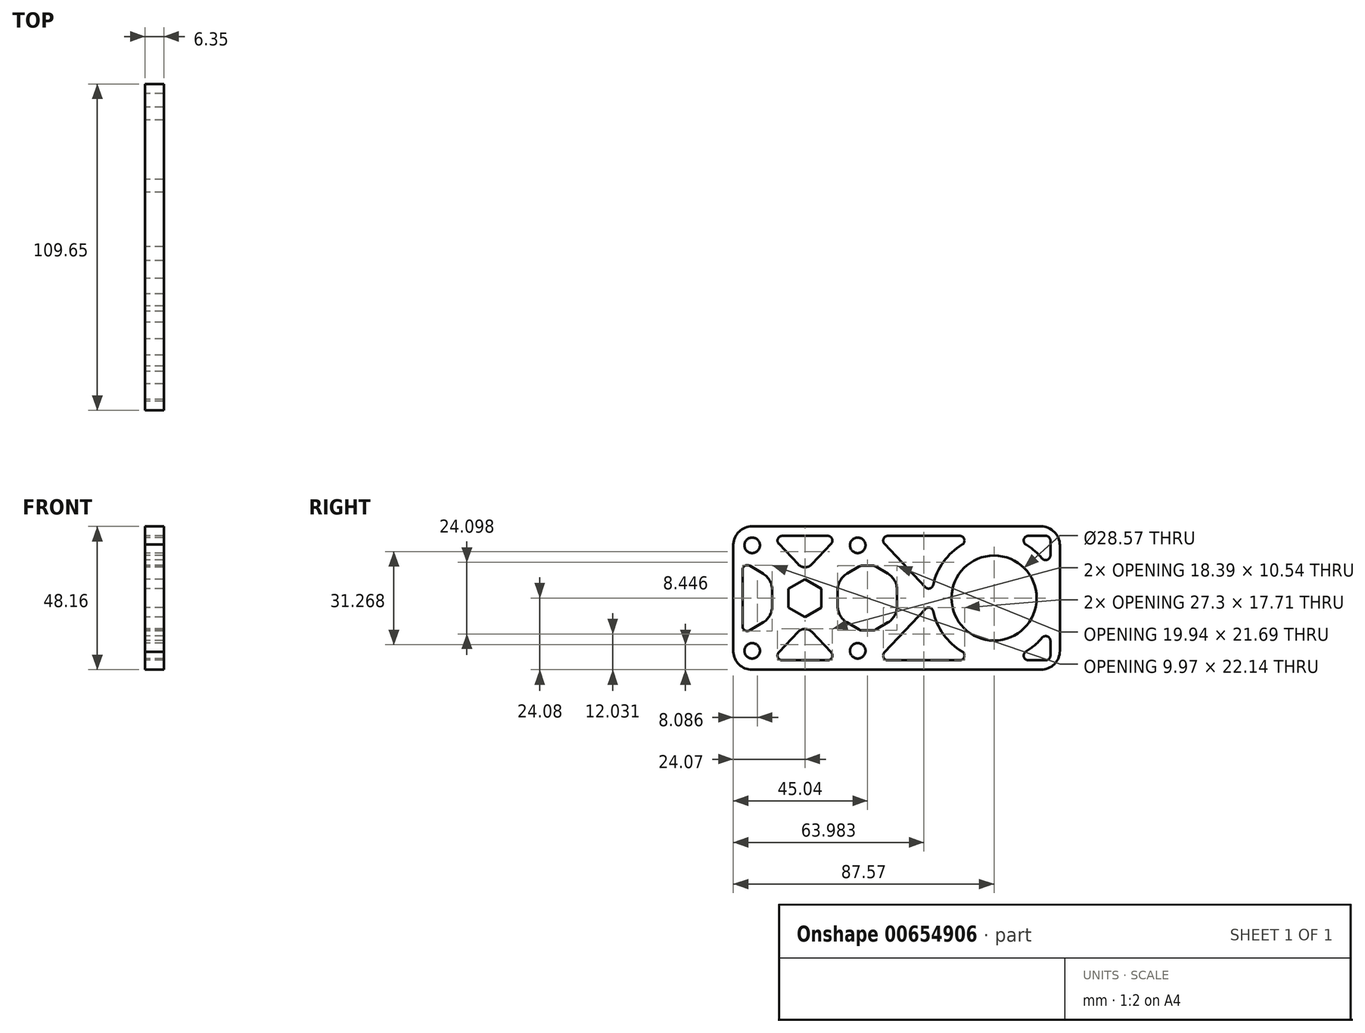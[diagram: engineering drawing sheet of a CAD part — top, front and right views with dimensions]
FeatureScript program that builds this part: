
annotation { "Feature Type Name" : "Feature", "Feature Type Description" : "" }
export const myFeature = defineFeature(function(context is Context, id is Id, definition is map)
    precondition{}
    {
        {
            var Q0;
            Q0=qCreatedBy(makeId("Right.planeOp"),FACE);
            var sketch = newSketch(context, id + "F0", { "sketchPlane" : qUnion([Q0])});
            skLineSegment(sketch, "E0", {"start": v(88.9, 0) * mm, "end": v(88.9, 101.6) * mm});
            skLineSegment(sketch, "E1", {"start": v(182.66, 0) * mm, "end": v(182.66, 330.2) * mm});
            skCircle(sketch, "E2", {"center": v(0, 0) * mm, "radius": 88.9 * mm});
            skCircle(sketch, "E3", {"center": v(63.5, 0) * mm, "radius": 14.29 * mm});
            skCircle(sketch, "E4.cCircle", {"center": v(0, 0) * mm, "radius": 6.35 * mm, "construction": true});
            skLineSegment(sketch, "E4.0", {"start": v(0, 6.35) * mm, "end": v(5.5, 3.18) * mm});
            skLineSegment(sketch, "E4.1", {"start": v(5.5, 3.18) * mm, "end": v(5.5, -3.17) * mm});
            skLineSegment(sketch, "E4.2", {"start": v(5.5, -3.17) * mm, "end": v(0, -6.35) * mm});
            skLineSegment(sketch, "E4.3", {"start": v(0, -6.35) * mm, "end": v(-5.5, -3.18) * mm});
            skLineSegment(sketch, "E4.4", {"start": v(-5.5, -3.18) * mm, "end": v(-5.5, 3.18) * mm});
            skLineSegment(sketch, "E4.5", {"start": v(-5.5, 3.18) * mm, "end": v(0, 6.35) * mm});
            skLineSegment(sketch, "E5", {"start": v(-102.68, -50.8) * mm, "end": v(111.05, -50.8) * mm});
            skCircle(sketch, "E6", {"center": v(17.73, 17.73) * mm, "radius": 2.6 * mm});
            skPoint(sketch, "E7.endSnap0", {"position": v(5.5, 0) * mm});
            skCircle(sketch, "E8.MirrorC", {"center": v(17.73, -17.73) * mm, "radius": 2.6 * mm});
            skCircle(sketch, "E9.MirrorC", {"center": v(-17.73, 17.73) * mm, "radius": 2.6 * mm});
            skCircle(sketch, "E10.MirrorC", {"center": v(-17.73, -17.73) * mm, "radius": 2.6 * mm});
            skArc(sketch, "E11", {"start": v(-24.07, -17.43) * mm, "mid": v(-22.33, -22.11) * mm, "end": v(-17.73, -24.08) * mm});
            skArc(sketch, "E12", {"start": v(-17.73, 24.08) * mm, "mid": v(-22.33, 22.11) * mm, "end": v(-24.07, 17.43) * mm});
            skLineSegment(sketch, "E13.1", {"start": v(11, 2.73) * mm, "end": v(11, -2.73) * mm});
            skLineSegment(sketch, "E13.4", {"start": v(-11, -2.73) * mm, "end": v(-11, 2.73) * mm});
            skPoint(sketch, "E14.orphan", {"position": v(0, 19.05) * mm});
            skLineSegment(sketch, "E15", {"start": v(-14.1, 8.2) * mm, "end": v(-18.57, 10.85) * mm});
            skLineSegment(sketch, "E16", {"start": v(14.1, 8.2) * mm, "end": v(18.2, 10.62) * mm});
            skLineSegment(sketch, "E17", {"start": v(14.1, -8.2) * mm, "end": v(18.2, -10.62) * mm});
            skLineSegment(sketch, "E18", {"start": v(-14.1, -8.2) * mm, "end": v(-18.57, -10.85) * mm});
            skLineSegment(sketch, "E19", {"start": v(-2.31, 11.36) * mm, "end": v(-8.78, 18.23) * mm});
            skPoint(sketch, "E20.visualSharp", {"position": v(0, 8.9) * mm});
            skArc(sketch, "E20.filletArc", {"start": v(-2.31, 11.36) * mm, "mid": v(-1.26, 10.62) * mm, "end": v(0, 10.36) * mm});
            skPoint(sketch, "E21.visualSharp", {"position": v(-11, 6.35) * mm});
            skArc(sketch, "E21.filletArc", {"start": v(-11, 2.73) * mm, "mid": v(-11.83, 5.88) * mm, "end": v(-14.1, 8.2) * mm});
            skPoint(sketch, "E22.visualSharp", {"position": v(-11, -6.35) * mm});
            skArc(sketch, "E22.filletArc", {"start": v(-14.1, -8.2) * mm, "mid": v(-11.83, -5.88) * mm, "end": v(-11, -2.73) * mm});
            skPoint(sketch, "E23.visualSharp", {"position": v(11, -6.35) * mm});
            skArc(sketch, "E23.filletArc", {"start": v(11, -2.73) * mm, "mid": v(11.83, -5.88) * mm, "end": v(14.1, -8.2) * mm});
            skPoint(sketch, "E24.visualSharp", {"position": v(11, 6.35) * mm});
            skArc(sketch, "E24.filletArc", {"start": v(14.1, 8.2) * mm, "mid": v(11.83, 5.88) * mm, "end": v(11, 2.73) * mm});
            skLineSegment(sketch, "E25", {"start": v(17.73, -24.08) * mm, "end": v(79.23, -24.08) * mm});
            skLineSegment(sketch, "E26", {"start": v(17.73, 24.08) * mm, "end": v(79.23, 24.08) * mm});
            skLineSegment(sketch, "E27.trimOffspring", {"start": v(88.9, 24.08) * mm, "end": v(94.09, 24.08) * mm});
            skLineSegment(sketch, "E28", {"start": v(85.58, -17.73) * mm, "end": v(85.58, 17.73) * mm});
            skArc(sketch, "E29", {"start": v(74.2, -17.95) * mm, "mid": v(77.1, -15.88) * mm, "end": v(79.6, -13.34) * mm});
            skLineSegment(sketch, "E30", {"start": v(17.73, 24.08) * mm, "end": v(-17.73, 24.08) * mm});
            skLineSegment(sketch, "E31", {"start": v(-7.62, 20.9) * mm, "end": v(0, 20.9) * mm});
            skLineSegment(sketch, "E32", {"start": v(-20.97, 9.48) * mm, "end": v(-20.97, -9.48) * mm});
            skLineSegment(sketch, "E33", {"start": v(-24.07, 18.03) * mm, "end": v(-24.07, -18.03) * mm});
            skLineSegment(sketch, "E34", {"start": v(17.73, -24.08) * mm, "end": v(-17.73, -24.08) * mm});
            skPoint(sketch, "E35.visualSharp", {"position": v(-11.3, 20.9) * mm});
            skArc(sketch, "E35.filletArc", {"start": v(-7.62, 20.9) * mm, "mid": v(-9.08, 19.95) * mm, "end": v(-8.78, 18.23) * mm});
            skPoint(sketch, "E36.visualSharp", {"position": v(-20.97, 12.27) * mm});
            skArc(sketch, "E36.filletArc", {"start": v(-18.57, 10.85) * mm, "mid": v(-20.17, 10.86) * mm, "end": v(-20.97, 9.48) * mm});
            skPoint(sketch, "E37.visualSharp", {"position": v(-20.97, -12.27) * mm});
            skArc(sketch, "E37.filletArc", {"start": v(-20.97, -9.48) * mm, "mid": v(-20.17, -10.86) * mm, "end": v(-18.57, -10.85) * mm});
            skPoint(sketch, "E38.visualSharp", {"position": v(20.97, 12.27) * mm});
            skPoint(sketch, "E39.visualSharp", {"position": v(20.97, -12.27) * mm});
            skLineSegment(sketch, "E40.MirrorCS", {"start": v(7.62, 20.9) * mm, "end": v(0, 20.9) * mm});
            skLineSegment(sketch, "E41.MirrorCS", {"start": v(2.31, 11.36) * mm, "end": v(8.78, 18.23) * mm});
            skArc(sketch, "E42.MirrorCS", {"start": v(2.31, 11.36) * mm, "mid": v(1.26, 10.62) * mm, "end": v(0, 10.36) * mm});
            skArc(sketch, "E43.MirrorCS", {"start": v(7.62, 20.9) * mm, "mid": v(9.08, 19.95) * mm, "end": v(8.78, 18.23) * mm});
            skArc(sketch, "E44.MirrorCS", {"start": v(2.31, -11.36) * mm, "mid": v(1.26, -10.62) * mm, "end": v(0, -10.36) * mm});
            skArc(sketch, "E45.MirrorCS", {"start": v(-2.31, -11.36) * mm, "mid": v(-1.26, -10.62) * mm, "end": v(0, -10.36) * mm});
            skLineSegment(sketch, "E46.MirrorCS", {"start": v(-2.31, -11.36) * mm, "end": v(-8.78, -18.23) * mm});
            skArc(sketch, "E47.MirrorCS", {"start": v(-7.62, -20.9) * mm, "mid": v(-9.08, -19.95) * mm, "end": v(-8.78, -18.23) * mm});
            skLineSegment(sketch, "E48.MirrorCS", {"start": v(-7.62, -20.9) * mm, "end": v(0, -20.9) * mm});
            skLineSegment(sketch, "E49.MirrorCS", {"start": v(7.62, -20.9) * mm, "end": v(0, -20.9) * mm});
            skArc(sketch, "E50.MirrorCS", {"start": v(7.62, -20.9) * mm, "mid": v(9.08, -19.95) * mm, "end": v(8.78, -18.23) * mm});
            skLineSegment(sketch, "E51.MirrorCS", {"start": v(2.31, -11.36) * mm, "end": v(8.78, -18.23) * mm});
            skLineSegment(sketch, "E52.MirrorCS", {"start": v(27.83, 8.2) * mm, "end": v(23.74, 10.62) * mm});
            skArc(sketch, "E53.MirrorCS", {"start": v(27.83, 8.2) * mm, "mid": v(30.11, 5.88) * mm, "end": v(30.94, 2.73) * mm});
            skLineSegment(sketch, "E54.MirrorCS", {"start": v(30.94, 2.73) * mm, "end": v(30.94, -2.73) * mm});
            skArc(sketch, "E55.MirrorCS", {"start": v(30.94, -2.73) * mm, "mid": v(30.11, -5.88) * mm, "end": v(27.83, -8.2) * mm});
            skLineSegment(sketch, "E56.MirrorCS", {"start": v(27.83, -8.2) * mm, "end": v(23.74, -10.62) * mm});
            skLineSegment(sketch, "E57", {"start": v(22.93, 10.85) * mm, "end": v(19, 10.85) * mm});
            skLineSegment(sketch, "E58", {"start": v(22.93, -10.85) * mm, "end": v(19, -10.85) * mm});
            skPoint(sketch, "E59.visualSharp", {"position": v(18.57, -10.85) * mm});
            skArc(sketch, "E59.filletArc", {"start": v(18.2, -10.62) * mm, "mid": v(18.59, -10.79) * mm, "end": v(19, -10.85) * mm});
            skPoint(sketch, "E60.visualSharp", {"position": v(23.37, -10.85) * mm});
            skArc(sketch, "E60.filletArc", {"start": v(22.93, -10.85) * mm, "mid": v(23.35, -10.79) * mm, "end": v(23.74, -10.62) * mm});
            skPoint(sketch, "E61.visualSharp", {"position": v(18.57, 10.85) * mm});
            skArc(sketch, "E61.filletArc", {"start": v(19, 10.85) * mm, "mid": v(18.59, 10.79) * mm, "end": v(18.2, 10.62) * mm});
            skPoint(sketch, "E62.visualSharp", {"position": v(23.37, 10.85) * mm});
            skArc(sketch, "E62.filletArc", {"start": v(23.74, 10.62) * mm, "mid": v(23.35, 10.79) * mm, "end": v(22.93, 10.85) * mm});
            skLineSegment(sketch, "E63", {"start": v(17.73, 17.73) * mm, "end": v(17.73, -17.73) * mm});
            skArc(sketch, "E64.MirrorCS", {"start": v(27.84, -20.9) * mm, "mid": v(26.38, -19.95) * mm, "end": v(26.68, -18.23) * mm});
            skLineSegment(sketch, "E65.MirrorCS", {"start": v(40.37, -3.7) * mm, "end": v(26.68, -18.23) * mm});
            skLineSegment(sketch, "E66", {"start": v(75.02, 20.9) * mm, "end": v(80.81, 20.9) * mm});
            skLineSegment(sketch, "E67", {"start": v(75.02, -20.9) * mm, "end": v(80.81, -20.9) * mm});
            skLineSegment(sketch, "E68", {"start": v(82.4, -19.32) * mm, "end": v(82.4, -14.36) * mm});
            skArc(sketch, "E69.trimOffspring", {"start": v(79.6, 13.34) * mm, "mid": v(77.1, 15.88) * mm, "end": v(74.2, 17.95) * mm});
            skLineSegment(sketch, "E70.trimOffspring", {"start": v(82.4, 14.36) * mm, "end": v(82.4, 19.32) * mm});
            skPoint(sketch, "E71.visualSharp", {"position": v(63.5, 20.9) * mm});
            skArc(sketch, "E71.filletArc", {"start": v(75.02, 20.9) * mm, "mid": v(73.5, 19.74) * mm, "end": v(74.2, 17.95) * mm});
            skPoint(sketch, "E72.visualSharp", {"position": v(82.4, 8.93) * mm});
            skArc(sketch, "E72.filletArc", {"start": v(79.6, 13.34) * mm, "mid": v(81.35, 12.86) * mm, "end": v(82.4, 14.36) * mm});
            skPoint(sketch, "E73.visualSharp", {"position": v(82.4, 20.9) * mm});
            skArc(sketch, "E73.filletArc", {"start": v(82.4, 19.32) * mm, "mid": v(81.94, 20.44) * mm, "end": v(80.81, 20.9) * mm});
            skPoint(sketch, "E74.visualSharp", {"position": v(82.4, -8.93) * mm});
            skArc(sketch, "E74.filletArc", {"start": v(82.4, -14.36) * mm, "mid": v(81.35, -12.86) * mm, "end": v(79.6, -13.34) * mm});
            skPoint(sketch, "E75.visualSharp", {"position": v(82.4, -20.9) * mm});
            skArc(sketch, "E75.filletArc", {"start": v(80.81, -20.9) * mm, "mid": v(81.94, -20.44) * mm, "end": v(82.4, -19.32) * mm});
            skPoint(sketch, "E76.visualSharp", {"position": v(63.5, -20.9) * mm});
            skArc(sketch, "E76.filletArc", {"start": v(74.2, -17.95) * mm, "mid": v(73.5, -19.74) * mm, "end": v(75.02, -20.9) * mm});
            skLineSegment(sketch, "E77", {"start": v(63.5, 0) * mm, "end": v(63.5, 20.9) * mm});
            skArc(sketch, "E78.MirrorCS", {"start": v(52.8, -17.95) * mm, "mid": v(53.5, -19.74) * mm, "end": v(51.98, -20.9) * mm});
            skArc(sketch, "E79", {"start": v(43.07, -4.44) * mm, "mid": v(46.53, -12.2) * mm, "end": v(52.8, -17.95) * mm});
            skPoint(sketch, "E80.orphan", {"position": v(33.15, -11.36) * mm});
            skPoint(sketch, "E81.visualSharp", {"position": v(42.64, -1.28) * mm});
            skArc(sketch, "E81.filletArc", {"start": v(43.07, -4.44) * mm, "mid": v(41.95, -3.25) * mm, "end": v(40.37, -3.7) * mm});
            skLineSegment(sketch, "E82", {"start": v(27.84, -20.9) * mm, "end": v(51.98, -20.9) * mm});
            skLineSegment(sketch, "E83", {"start": v(63.5, 0) * mm, "end": v(54.03, 0) * mm});
            skArc(sketch, "E84.MirrorCS", {"start": v(43.07, 4.44) * mm, "mid": v(41.95, 3.25) * mm, "end": v(40.37, 3.7) * mm});
            skArc(sketch, "E85.MirrorCS", {"start": v(43.07, 4.44) * mm, "mid": v(46.53, 12.2) * mm, "end": v(52.8, 17.95) * mm});
            skArc(sketch, "E86.MirrorCS", {"start": v(52.8, 17.95) * mm, "mid": v(53.5, 19.74) * mm, "end": v(51.98, 20.9) * mm});
            skLineSegment(sketch, "E87.MirrorCS", {"start": v(27.84, 20.9) * mm, "end": v(51.98, 20.9) * mm});
            skArc(sketch, "E88.MirrorCS", {"start": v(27.84, 20.9) * mm, "mid": v(26.38, 19.95) * mm, "end": v(26.68, 18.23) * mm});
            skLineSegment(sketch, "E89.MirrorCS", {"start": v(40.37, 3.7) * mm, "end": v(26.68, 18.23) * mm});
            skPoint(sketch, "E90.visualSharp", {"position": v(85.58, 24.08) * mm});
            skArc(sketch, "E90.filletArc", {"start": v(85.58, 17.73) * mm, "mid": v(83.72, 22.22) * mm, "end": v(79.23, 24.08) * mm});
            skPoint(sketch, "E91.visualSharp", {"position": v(85.58, -24.08) * mm});
            skArc(sketch, "E91.filletArc", {"start": v(79.23, -24.08) * mm, "mid": v(83.72, -22.22) * mm, "end": v(85.58, -17.73) * mm});
            skSolve(sketch);
        }
        {
            var Q0;
            Q0=makeQuery(id+"F0.imprint","IMPRINT",FACE,{"disambiguationData":[TD([[makeQuery(id+"F0.imprint","IMPRINT",EDGE,{"derivedFrom":sQuery(id+"F0.wireOp",EDGE,"E3")}),-1.0]])]});
            extrude(context, id + "F1", {"entities" : qUnion([Q0]), "depth" : 6.35 * mm, "offsetDistance" : 25.4 * mm});
        }
    });
